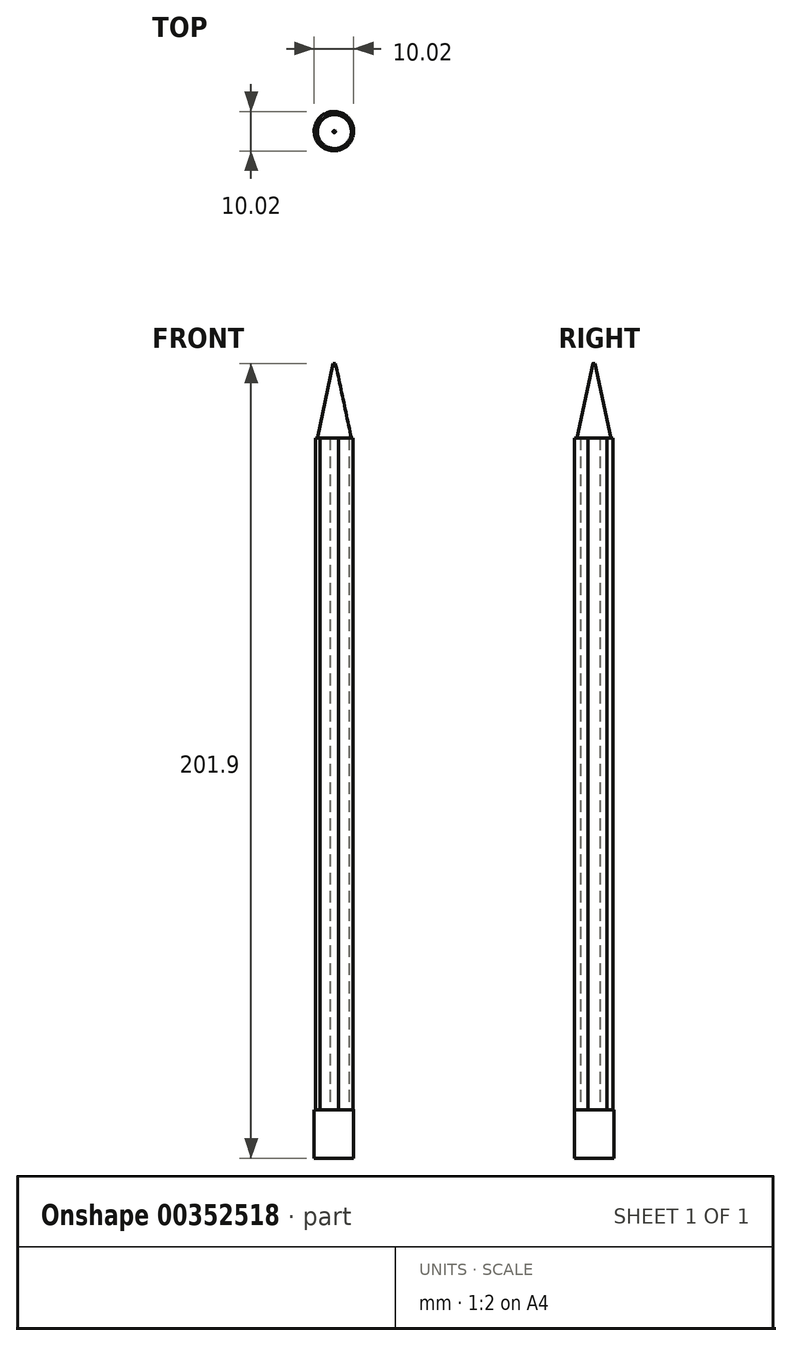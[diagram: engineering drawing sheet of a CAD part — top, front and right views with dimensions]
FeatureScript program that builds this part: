
annotation { "Feature Type Name" : "Feature", "Feature Type Description" : "" }
export const myFeature = defineFeature(function(context is Context, id is Id, definition is map)
    precondition{}
    {
        {
            var Q0;
            Q0=qCreatedBy(makeId("Top.planeOp"),FACE);
            var sketch = newSketch(context, id + "F0", { "sketchPlane" : qUnion([Q0])});
            skCircle(sketch, "E0.cCircle", {"center": v(-16.9, 22.4) * mm, "radius": 4.33 * mm, "construction": true});
            skLineSegment(sketch, "E0.0", {"start": v(-12.12, 20.9) * mm, "end": v(-15.8, 17.51) * mm});
            skLineSegment(sketch, "E0.1", {"start": v(-15.8, 17.51) * mm, "end": v(-20.57, 19) * mm});
            skLineSegment(sketch, "E0.2", {"start": v(-20.57, 19) * mm, "end": v(-21.67, 23.89) * mm});
            skLineSegment(sketch, "E0.3", {"start": v(-21.67, 23.89) * mm, "end": v(-17.99, 27.27) * mm});
            skLineSegment(sketch, "E0.4", {"start": v(-17.99, 27.27) * mm, "end": v(-13.22, 25.78) * mm});
            skLineSegment(sketch, "E0.5", {"start": v(-13.22, 25.78) * mm, "end": v(-12.12, 20.9) * mm});
            skPoint(sketch, "E0.0.midPoint", {"position": v(-13.96, 19.2) * mm});
            skSolve(sketch);
        }
        {
            var Q0;
            Q0 = qSketchRegion(id + "F0", true);
            extrude(context, id + "F1", {"entities" : qUnion([Q0]), "depth" : 170.6 * mm});
        }
        {
            var Q0;
            Q0=makeQuery(id+"F1.opExtrude","CAP_FACE",FACE,{"disambiguationData":[OSD([sQuery(id+"F0.wireOp",EDGE,"E0.0"),sQuery(id+"F0.wireOp",EDGE,"E0.1"),sQuery(id+"F0.wireOp",EDGE,"E0.2"),sQuery(id+"F0.wireOp",EDGE,"E0.3"),sQuery(id+"F0.wireOp",EDGE,"E0.4"),sQuery(id+"F0.wireOp",EDGE,"E0.5")])],"isStart":true});
            var sketch = newSketch(context, id + "F2", { "sketchPlane" : qUnion([Q0])});
            skCircle(sketch, "E1", {"center": v(-17, -22.5) * mm, "radius": 5.01 * mm});
            skSolve(sketch);
        }
        {
            var Q0;
            Q0 = qSketchRegion(id + "F2", true);
            extrude(context, id + "F3", {"entities" : qUnion([Q0]), "operationType" : NewBodyOperationType.ADD, "depth" : 12.3 * mm});
        }
        {
            var Q0;
            Q0=makeQuery(id+"F1.opExtrude","CAP_FACE",FACE,{"disambiguationData":[OSD([sQuery(id+"F0.wireOp",EDGE,"E0.0"),sQuery(id+"F0.wireOp",EDGE,"E0.1"),sQuery(id+"F0.wireOp",EDGE,"E0.2"),sQuery(id+"F0.wireOp",EDGE,"E0.3"),sQuery(id+"F0.wireOp",EDGE,"E0.4"),sQuery(id+"F0.wireOp",EDGE,"E0.5")])],"isStart":false});
            var sketch = newSketch(context, id + "F4", { "sketchPlane" : qUnion([Q0])});
            skLineSegment(sketch, "E2", {"start": v(-20.57, 19) * mm, "end": v(-13.22, 25.78) * mm});
            skCircle(sketch, "E3", {"center": v(-16.9, 22.4) * mm, "radius": 4.33 * mm});
            skSolve(sketch);
        }
        {
            var Q0;
            Q0 = qSketchRegion(id + "F4", true);
            extrude(context, id + "F5", {"entities" : qUnion([Q0]), "operationType" : NewBodyOperationType.ADD, "depth" : 19 * mm, "hasDraft" : true, "draftAngle" : 12 * degree, "draftPullDirection" : true});
        }
    });
